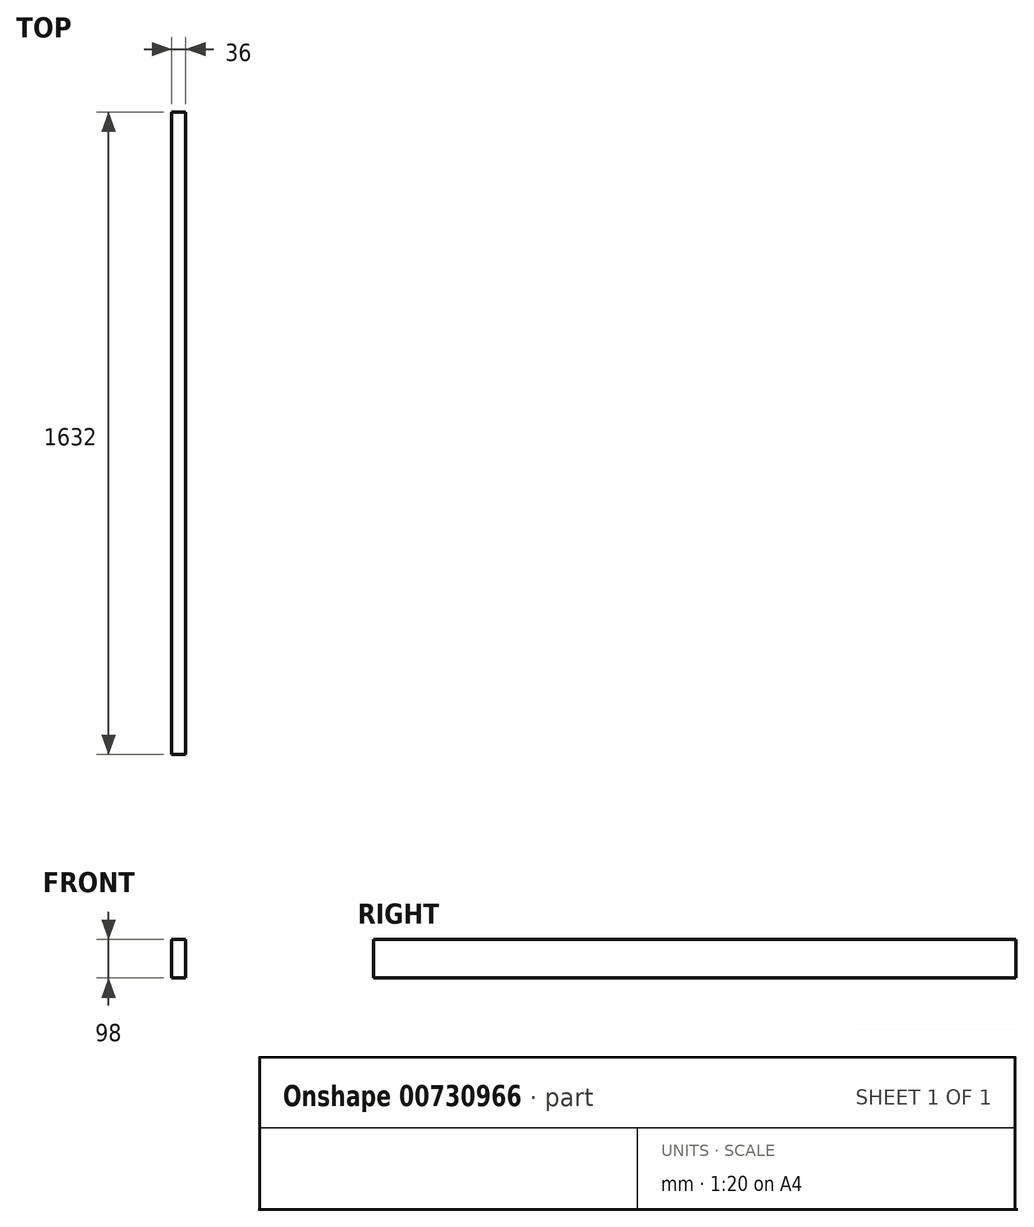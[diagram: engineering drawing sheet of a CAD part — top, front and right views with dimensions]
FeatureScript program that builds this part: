
annotation { "Feature Type Name" : "Feature", "Feature Type Description" : "" }
export const myFeature = defineFeature(function(context is Context, id is Id, definition is map)
    precondition{}
    {
        {
            var Q0;
            Q0=qCreatedBy(makeId("Front.planeOp"),FACE);
            var sketch = newSketch(context, id + "F0", { "sketchPlane" : qUnion([Q0])});
            skLineSegment(sketch, "E0.bottom", {"start": v(18, -49) * mm, "end": v(-18, -49) * mm});
            skLineSegment(sketch, "E0.top", {"start": v(18, 49) * mm, "end": v(-18, 49) * mm});
            skLineSegment(sketch, "E0.left", {"start": v(18, -49) * mm, "end": v(18, 49) * mm});
            skLineSegment(sketch, "E0.right", {"start": v(-18, -49) * mm, "end": v(-18, 49) * mm});
            skPoint(sketch, "E0.middle", {"position": v(0, 0) * mm});
            skSolve(sketch);
        }
        {
            var Q0;
            Q0=makeQuery(id+"F0.imprint","IMPRINT",FACE,{"disambiguationData":[TD([[makeQuery(id+"F0.imprint","IMPRINT",EDGE,{"derivedFrom":sQuery(id+"F0.wireOp",EDGE,"E0.bottom")}),-1.0]])]});
            extrude(context, id + "F1", {"entities" : qUnion([Q0]), "depth" : 1632 * mm, "offsetDistance" : 25 * mm});
        }
    });
